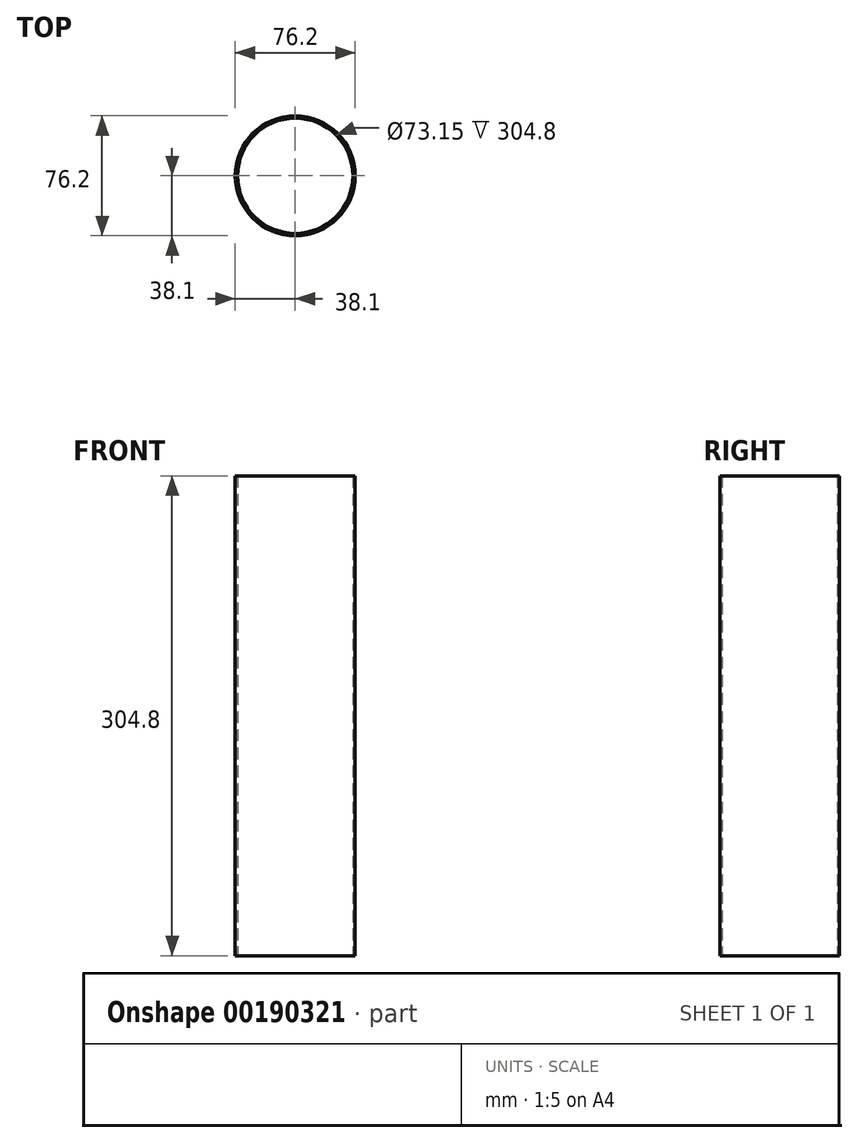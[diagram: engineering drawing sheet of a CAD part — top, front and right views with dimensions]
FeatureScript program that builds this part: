
annotation { "Feature Type Name" : "Feature", "Feature Type Description" : "" }
export const myFeature = defineFeature(function(context is Context, id is Id, definition is map)
    precondition{}
    {
        {
            var Q0;
            Q0=qCreatedBy(makeId("Top.planeOp"),FACE);
            var sketch = newSketch(context, id + "F0", { "sketchPlane" : qUnion([Q0])});
            skCircle(sketch, "E0", {"center": v(0, 0) * mm, "radius": 38.1 * mm});
            skCircle(sketch, "E1.0", {"center": v(0, 0) * mm, "radius": 36.58 * mm});
            skSolve(sketch);
        }
        {
            var Q0;
            Q0=makeQuery(id+"F0.imprint","IMPRINT",FACE,{"disambiguationData":[TD([[makeQuery(id+"F0.imprint","IMPRINT",EDGE,{"derivedFrom":sQuery(id+"F0.wireOp",EDGE,"E0")}),1.0]])]});
            extrude(context, id + "F1", {"entities" : qUnion([Q0]), "depth" : 304.8 * mm});
        }
    });
